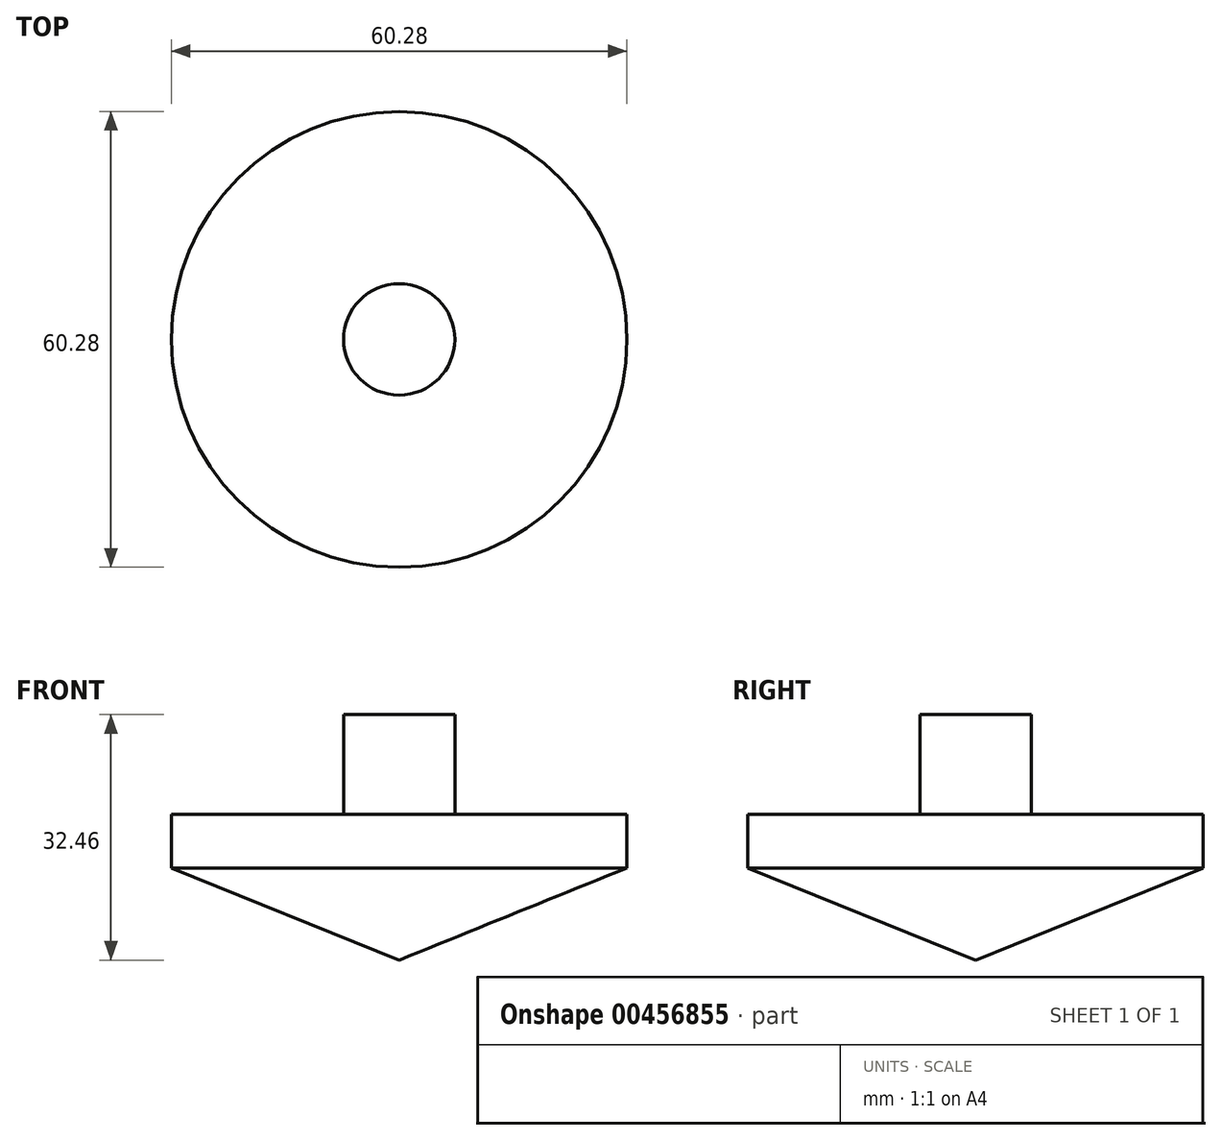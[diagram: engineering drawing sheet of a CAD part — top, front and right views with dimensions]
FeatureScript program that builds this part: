
annotation { "Feature Type Name" : "Feature", "Feature Type Description" : "" }
export const myFeature = defineFeature(function(context is Context, id is Id, definition is map)
    precondition{}
    {
        {
            var Q0;
            Q0=qCreatedBy(makeId("Front.planeOp"),FACE);
            var sketch = newSketch(context, id + "F0", { "sketchPlane" : qUnion([Q0])});
            skLineSegment(sketch, "E0", {"start": v(0, 0) * mm, "end": v(30.14, 12.2) * mm});
            skLineSegment(sketch, "E1", {"start": v(30.14, 12.2) * mm, "end": v(30.14, 19.25) * mm});
            skLineSegment(sketch, "E2", {"start": v(30.14, 19.25) * mm, "end": v(7.37, 19.25) * mm});
            skLineSegment(sketch, "E3", {"start": v(7.37, 19.25) * mm, "end": v(7.37, 32.46) * mm});
            skLineSegment(sketch, "E4", {"start": v(7.37, 32.46) * mm, "end": v(0, 32.46) * mm});
            skLineSegment(sketch, "E5", {"start": v(0, 0) * mm, "end": v(0, 32.46) * mm});
            skSolve(sketch);
        }
        {
            var Q0;
            Q0 = qSketchRegion(id + "F0", true);
            var Q1;
            Q1=sQuery(id+"F0.wireOp",EDGE,"E5");
            revolve(context, id + "F1", {"entities" : qUnion([Q0]), "axis" : qUnion([Q1]), "revolveType" : RevolveType.FULL});
        }
    });
